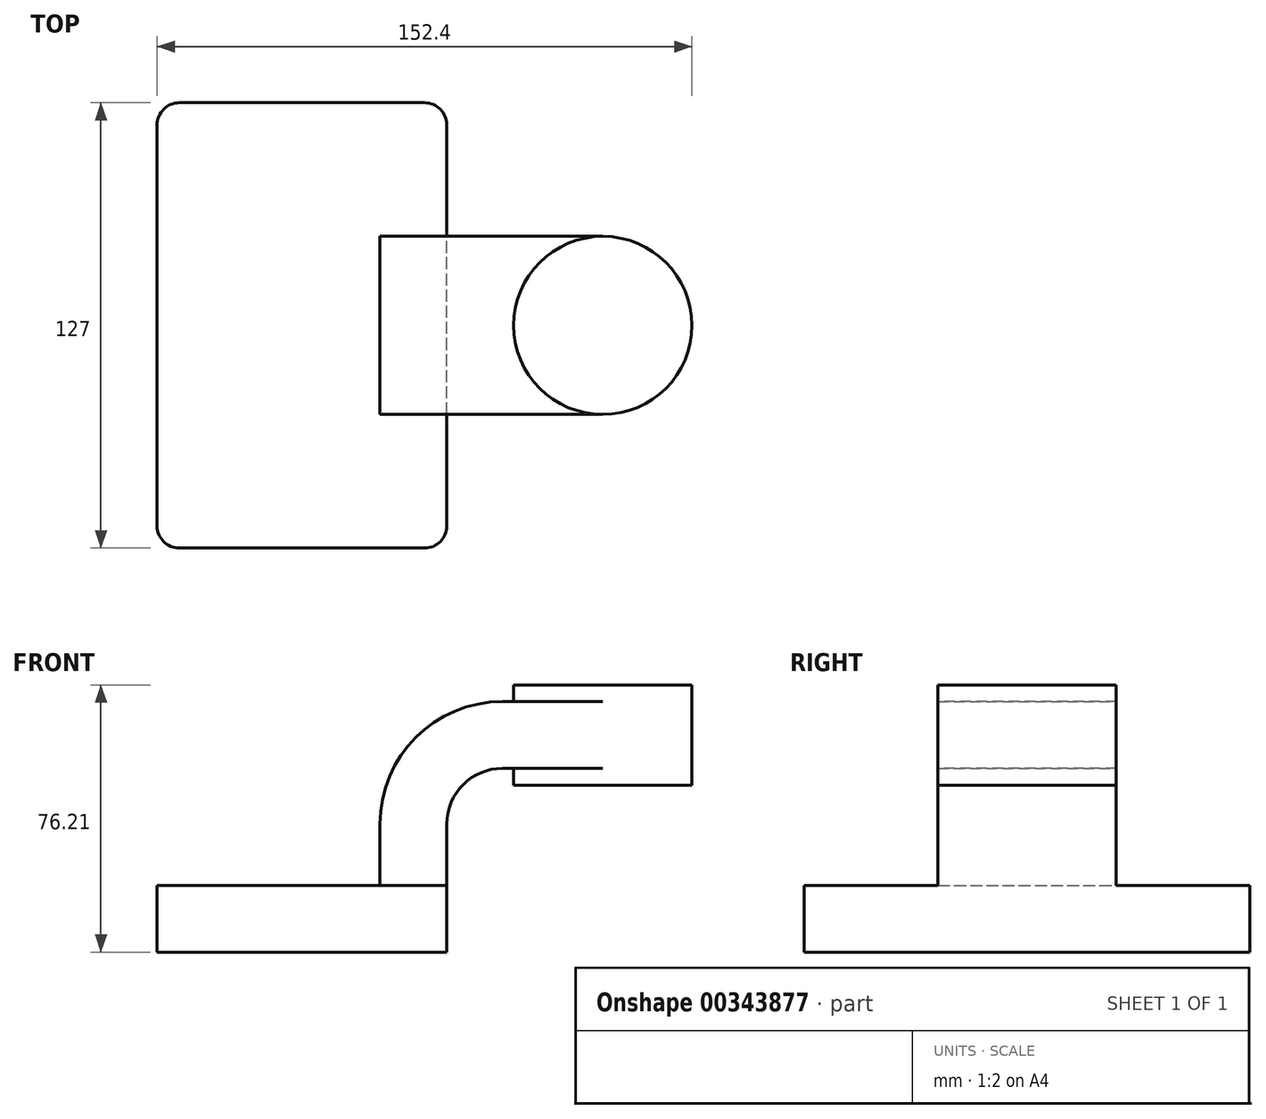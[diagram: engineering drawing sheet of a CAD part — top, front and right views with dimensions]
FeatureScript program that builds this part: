
annotation { "Feature Type Name" : "Feature", "Feature Type Description" : "" }
export const myFeature = defineFeature(function(context is Context, id is Id, definition is map)
    precondition{}
    {
        {
            var Q0;
            Q0=qCreatedBy(makeId("Front.planeOp"),FACE);
            var sketch = newSketch(context, id + "F0", { "sketchPlane" : qUnion([Q0])});
            skLineSegment(sketch, "E0.bottom", {"start": v(41.27, -9.52) * mm, "end": v(-41.27, -9.53) * mm});
            skLineSegment(sketch, "E0.top", {"start": v(41.27, 9.53) * mm, "end": v(-41.28, 9.53) * mm});
            skLineSegment(sketch, "E0.left", {"start": v(41.27, -9.52) * mm, "end": v(41.27, 9.53) * mm});
            skLineSegment(sketch, "E0.right", {"start": v(-41.28, -9.52) * mm, "end": v(-41.28, 9.53) * mm});
            skPoint(sketch, "E0.middle", {"position": v(0, 0) * mm});
            skLineSegment(sketch, "E1.bottom", {"start": v(60.32, 66.68) * mm, "end": v(111.12, 66.68) * mm});
            skLineSegment(sketch, "E1.top", {"start": v(60.32, 38.1) * mm, "end": v(111.12, 38.1) * mm});
            skLineSegment(sketch, "E1.left", {"start": v(60.32, 66.68) * mm, "end": v(60.32, 38.1) * mm});
            skLineSegment(sketch, "E1.right", {"start": v(111.12, 66.68) * mm, "end": v(111.12, 38.1) * mm});
            skPoint(sketch, "E1.middle", {"position": v(85.72, 52.39) * mm});
            skLineSegment(sketch, "E2", {"start": v(41.27, 9.53) * mm, "end": v(41.27, 27) * mm});
            skArc(sketch, "E3", {"start": v(41.27, 27) * mm, "mid": v(45.92, 38.23) * mm, "end": v(57.15, 42.88) * mm});
            skLineSegment(sketch, "E4", {"start": v(57.15, 42.88) * mm, "end": v(85.72, 42.88) * mm});
            skLineSegment(sketch, "E5.0", {"start": v(57.15, 61.93) * mm, "end": v(85.72, 61.93) * mm});
            skArc(sketch, "E5.1", {"start": v(22.22, 27) * mm, "mid": v(32.45, 51.7) * mm, "end": v(57.15, 61.93) * mm});
            skLineSegment(sketch, "E5.2", {"start": v(22.22, 9.53) * mm, "end": v(22.22, 27) * mm});
            skLineSegment(sketch, "E6", {"start": v(85.72, 42.88) * mm, "end": v(85.72, 52.39) * mm});
            skLineSegment(sketch, "E7", {"start": v(85.72, 52.39) * mm, "end": v(85.72, 61.93) * mm});
            skLineSegment(sketch, "E8", {"start": v(85.72, 61.93) * mm, "end": v(85.72, 66.68) * mm});
            skFitSpline(sketch, "E9", {"points": [v(-41.28, 9.53) * mm, v(57.15, 61.93) * mm], "startDerivative": vector(75.06, 29.47) * mm, "endDerivative": vector(129.55, -19.23) * mm});
            skLineSegment(sketch, "E10", {"start": v(85.72, 42.88) * mm, "end": v(85.72, 38.1) * mm});
            skSolve(sketch);
        }
        {
            var Q0;
            Q0=makeQuery(id+"F0.imprint","IMPRINT",FACE,{"disambiguationData":[TD([[makeQuery(id+"F0.imprint","IMPRINT",EDGE,{"derivedFrom":sQuery(id+"F0.wireOp",EDGE,"E0.bottom")}),-1.0]])]});
            extrude(context, id + "F1", {"entities" : qUnion([Q0]), "endBound" : BoundingType.SYMMETRIC, "depth" : 127 * mm});
        }
        {
            var Q0;
            {var subQ1=sQuery(id+"F0.wireOp",EDGE,"E2");Q0=makeQuery(id+"F0.imprint","IMPRINT",FACE,{"disambiguationData":[TD([[makeQuery(id+"F0.imprint","IMPRINT",EDGE,{"derivedFrom":subQ1}),1.0]])]});}
            var Q1;
            {var subQ4=sQuery(id+"F0.wireOp",EDGE,"E6");Q1=makeQuery(id+"F0.imprint","IMPRINT",FACE,{"disambiguationData":[TD([[makeQuery(id+"F0.imprint","IMPRINT",EDGE,{"derivedFrom":subQ4}),1.0]])]});}
            extrude(context, id + "F2", {"entities" : qUnion([Q0, Q1]), "operationType" : NewBodyOperationType.ADD, "endBound" : BoundingType.SYMMETRIC, "depth" : 50.8 * mm});
        }
        {
            var Q0;
            Q0=makeQuery(id+"F0.imprint","IMPRINT",FACE,{"disambiguationData":[TD([[makeQuery(id+"F0.imprint","IMPRINT",EDGE,{"derivedFrom":sQuery(id+"F0.wireOp",EDGE,"E5.1")}),1.0]])]});
            extrude(context, id + "F3", {"entities" : qUnion([Q0]), "operationType" : NewBodyOperationType.ADD, "endBound" : BoundingType.SYMMETRIC, "depth" : 15.88 * mm});
        }
        {
            var Q0;
            {var subQ0=sQuery(id+"F0.wireOp",EDGE,"E1.right");Q0=makeQuery(id+"F0.imprint","IMPRINT",FACE,{"disambiguationData":[TD([[makeQuery(id+"F0.imprint","IMPRINT",EDGE,{"derivedFrom":subQ0}),-1.0]])]});}
            var Q1;
            Q1=sQuery(id+"F0.wireOp",EDGE,"E10");
            revolve(context, id + "F4", {"operationType" : NewBodyOperationType.ADD, "entities" : qUnion([Q0]), "axis" : qUnion([Q1]), "revolveType" : RevolveType.FULL});
        }
        {
            var Q0;
            Q0=makeQuery(id+"F1.opExtrude","CAP_EDGE",EDGE,{"disambiguationData":[OSD([sQuery(id+"F0.wireOp",EDGE,"E0.left")])],"isStart":true});
            var Q1;
            Q1=makeQuery(id+"F1.opExtrude","CAP_EDGE",EDGE,{"disambiguationData":[OSD([sQuery(id+"F0.wireOp",EDGE,"E0.right")])],"isStart":true});
            var Q2;
            Q2=makeQuery(id+"F1.opExtrude","CAP_EDGE",EDGE,{"disambiguationData":[OSD([sQuery(id+"F0.wireOp",EDGE,"E0.right")])],"isStart":false});
            var Q3;
            Q3=makeQuery(id+"F1.opExtrude","CAP_EDGE",EDGE,{"disambiguationData":[OSD([sQuery(id+"F0.wireOp",EDGE,"E0.left")])],"isStart":false});
            fillet(context, id + "F5", {"entities" : qUnion([Q0, Q1, Q2, Q3]), "radius" : 6.35 * mm, "tangentPropagation" : true, "allowEdgeOverflow" : false});
        }
    });
